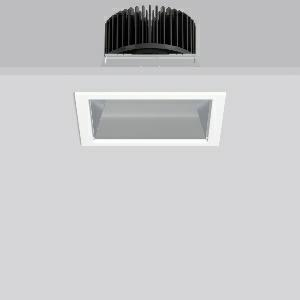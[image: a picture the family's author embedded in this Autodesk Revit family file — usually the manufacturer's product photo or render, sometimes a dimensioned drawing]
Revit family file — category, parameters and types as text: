
# Revit family: quardo_901705_002_1_4c05
name_source: partatom
category: Lighting Fixtures
units: mm (PartAtom-declared; Revit-internal decimal feet)

## family parameters
Cut with Voids When Loaded = No
Host = Face
Light Source = No
Part Type = Normal
Room Calculation Point = No
Round Connector Dimension = Use Diameter
Shared = No

## types (1)
- QUARDO (1 x LED Modul 840, 2600 lm, 4000)
    Apparent Load = 19 VA
    CIE Flux Codes = 80 100 100 100 100
    Color Rendering = 80
    Color Temperature = 4000
    Default Elevation = 1800 mm
    Description = Series: QUARDO
High-quality recessed downlight with square luminous surface. Recessed mounting frame: die-cast aluminium, powder-coated. Mounting bracket: galvanised sheet steel. Reflector: aluminium, highly polished anodised finish. Ceiling installation with spring system. Including separate LED converter with connecting cable 600 mm. Through-wiring box (5 pole) available as accessory. 
Colour: traffic white, matt (RAL 9016)
Length: 176 mm
Width: 176 mm
Height: 4 mm
Cut-out length: 165 mm
Cut-out width: 165 mm
Recess height: 150 mm
Luminaire: recess height: 145 mm
Lamp: LED
Socket: without socket
Colour temperature: 4000K
Colour rendering index (CRI): 85
System power: 19 W
Rated luminous flux: 2600 lm
Luminous efficiency: 137 lm/W
Control gear: Regulated power supply
Protection class: II
Type of protection: IP 20
    Height = 0 mm  [stored 0 ft]
    Lamp = 1 x LED Modul 840
    Lamp Light Flux = 2600 lm
    Lamp count = 1
    Length = 176 mm
    Lifetime = 50000 h
    Luminous efficacy = 137 lm/W
    Manufacturer = RZB
    ModVariant = No
    Model = 901705.002.1
    Mounting Place = Ceiling
    Mounting Type = Recessed
    Number of Poles = 1
    OnlyDefault = Yes
    Power Factor = 1
    Product Name = QUARDO
    Product group = Recessed downlights
    ProductGroupID = 402
    Protection Class = Protection class II
    Protection Degree = IP 20
    RLX_Detail_Level = 1
    RLX_Emergency_Light_Flux = 0 lm
    RLX_Emergency_Type = 0
    RLX_Emergency_Type_DB = No
    RlxData = <blob elided: 29357 chars, md5=6013304b>
    Socket = socket
    Standby Power = 0 W
    System Light Flux = 2600 lm
    System Power = 19 W
    Type Comments = Product without accessories
    Type Image = 901705.002.jpg
    URL = http://relux.com
    VarID = ---
    Voltage = 230 V
    Voltage Range = 220-240 V
    Weight = 0.00 kg
    Width = 176 mm

note: [stored X ft] marks values corroborated as IEEE doubles in the binary element streams (Revit-internal decimal feet)

## geometry (parser evidence)
native form markers: Blend x4, Sweep x10
no freeform markers — native parametric forms only
